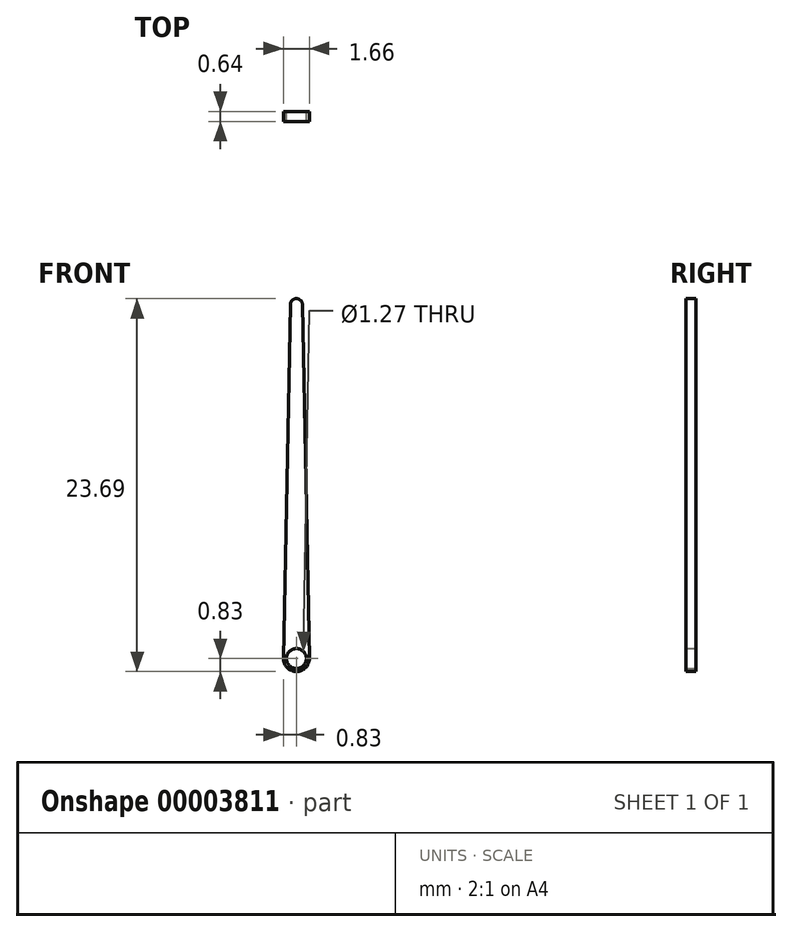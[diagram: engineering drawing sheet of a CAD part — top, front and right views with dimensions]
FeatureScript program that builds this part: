
annotation { "Feature Type Name" : "Feature", "Feature Type Description" : "" }
export const myFeature = defineFeature(function(context is Context, id is Id, definition is map)
    precondition{}
    {
        {
            var Q0;
            Q0=qCreatedBy(makeId("Front.planeOp"),FACE);
            var sketch = newSketch(context, id + "F0", { "sketchPlane" : qUnion([Q0])});
            skCircle(sketch, "E0", {"center": v(0, 0) * mm, "radius": 0.83 * mm});
            skPoint(sketch, "E1.start.orphan", {"position": v(0, 22.86) * mm});
            skPoint(sketch, "E2.orphan", {"position": v(-0.95, 0) * mm});
            skLineSegment(sketch, "E3", {"start": v(0, 0) * mm, "end": v(0, 25.4) * mm, "construction": true});
            skLineSegment(sketch, "E4", {"start": v(0, 22.86) * mm, "end": v(0, 22.86) * mm});
            skLineSegment(sketch, "E5", {"start": v(0.39, 22.48) * mm, "end": v(0.83, 0) * mm});
            skPoint(sketch, "E6.visualSharp", {"position": v(0.38, 22.86) * mm});
            skArc(sketch, "E6.filletArc", {"start": v(0.39, 22.48) * mm, "mid": v(0.27, 22.75) * mm, "end": v(0, 22.86) * mm});
            skArc(sketch, "E7.0.MirrorCS", {"start": v(-0.39, 22.48) * mm, "mid": v(-0.27, 22.75) * mm, "end": v(0, 22.86) * mm});
            skLineSegment(sketch, "E8.0.MirrorCS", {"start": v(-0.39, 22.48) * mm, "end": v(-0.83, 0) * mm});
            skSolve(sketch);
        }
        {
            var Q0;
            Q0=qSketchRegion(id+"F0",true);
            extrude(context, id + "F1", {"entities" : qUnion([Q0]), "depth" : 0.64 * mm});
        }
        {
            var Q0;
            {var subQ0=sQuery(id+"F0.wireOp",EDGE,"E0");var subQ2=makeQuery(id+"F0.imprint","INTERSECT",VERTEX,{"derivedFrom":[subQ0,sQuery(id+"F0.wireOp",EDGE,"E5")]});Q0=makeQuery(id+"F0.imprint","IMPRINT",FACE,{"disambiguationData":[TD([[makeQuery(id+"F0.imprint","IMPRINT",EDGE,{"disambiguationData":[TD([[subQ2,-1.0]])],"derivedFrom":subQ0}),1.0]])]});}
            var sketch = newSketch(context, id + "F2", { "sketchPlane" : qUnion([Q0])});
            skCircle(sketch, "E9", {"center": v(0, 0) * mm, "radius": 0.64 * mm});
            skSolve(sketch);
        }
        {
            var Q0;
            Q0=makeQuery(id+"F2.imprint","IMPRINT",FACE,{"disambiguationData":[TD([[makeQuery(id+"F2.imprint","IMPRINT",EDGE,{"derivedFrom":sQuery(id+"F2.wireOp",EDGE,"E9")}),1.0]])]});
            extrude(context, id + "F3", {"entities" : qUnion([Q0]), "operationType" : NewBodyOperationType.REMOVE, "depth" : 25.4 * mm});
        }
    });
